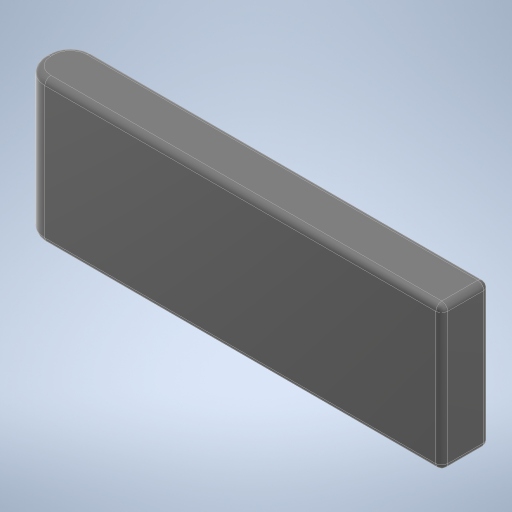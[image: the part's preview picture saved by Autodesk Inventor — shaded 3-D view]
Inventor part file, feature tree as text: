
AUTODESK INVENTOR PART (.ipt)
format: ipt  version: 2024.2 (Build 282272000, 272)  size: 233,472 bytes
history: native  units: mm
features: fillet x2, extrude x1, sketch x1
ambient origin geometry x8: Origin, YZ Plane, XZ Plane, XY Plane, X Axis, Y Axis, Z Axis, Center Point
bodies: Solid1 (feature_tree)
feature tree (4):
  extrude  "Extrusion1"  Depth=140.0mm
  fillet  "Fillet1"  Radius=48.0mm
  fillet  "Fillet2"  Radius=2.0mm
  sketch  "Sketch1"  dims[d0=16.0mm d1=140.0mm d2=48.0mm d3=0.0mm d4=2.0mm d5=7.5mm]
